# Revit family: Zumtobel SCON-S
name_source: partatom
category: Leuchten
revit_build: Autodesk Revit 2016 (Build: 20150714_1515(x64)
units: mm (PartAtom-declared; Revit-internal decimal feet)

## family parameters
Basisbauteil = Fläche
Beim Laden mit Abzugskörper schneiden = Nein
Bemaßung runder Anschluss = Durchmesser verwenden
Gemeinsam genutzt = Nein
Lichtquelle = Ja
OmniClass-Nummer = 23.80.70.11
OmniClass-Titel = Luminaries for Internal Lighting
Raumberechnungspunkt = Nein
Teiletyp = Normal

## types (3) — shared parameters
Baugruppenkennzeichen = D5020210
Beschreibung = Pendant luminaire
Emissionsform beim Rendern sichtbar = Ja
Farbfilter = 16777215
Farbtemperaturverschiebung bei Dämpfen der Lampe = <Keine Auswahl>
Hersteller = Zumtobel Lighting
Neigungswinkel = -90.00°
URL = http://www.zumtobel.com
Von Kreisdurchmesser aussenden = 70 mm
zero-valued in all types: Vorgabe-Ansicht

## per-type parameters (varying)
| type | Datei für fotometrisches Netz | Height | Lampe | Length | Modell | Scheinlast | Scon 250 | Scon 500 | Width |
| SCON-S 250 1/7,5W LED | ST6177_A.IES | 250 mm  [stored 0.82021 ft] | LED | 250 mm  [stored 0.82021 ft] | 60510062 | 10 VA | Ja | Nein | 250 mm  [stored 0.82021 ft] |
| SCON-S 500 1/23W TCG-SE CR | 60510021_(STD_LEO).IES | 390 mm  [stored 1.27953 ft] | TCG-SE | 500 mm  [stored 1.64042 ft] | 60510021 | 21 VA | Nein | Ja | 500 mm  [stored 1.64042 ft] |
| SCON-S 170 | ST8366_N.IES | 154 mm  [stored 0.505249 ft] | TCG-SE | 170 mm  [stored 0.557743 ft] | 60510021 | 9 VA | Nein | Ja | 170 mm  [stored 0.557743 ft] |

note: [stored X ft] marks values corroborated as IEEE doubles in the binary element streams (Revit-internal decimal feet)

## geometry (parser evidence)
native form markers: Sweep x3
no freeform markers — native parametric forms only
